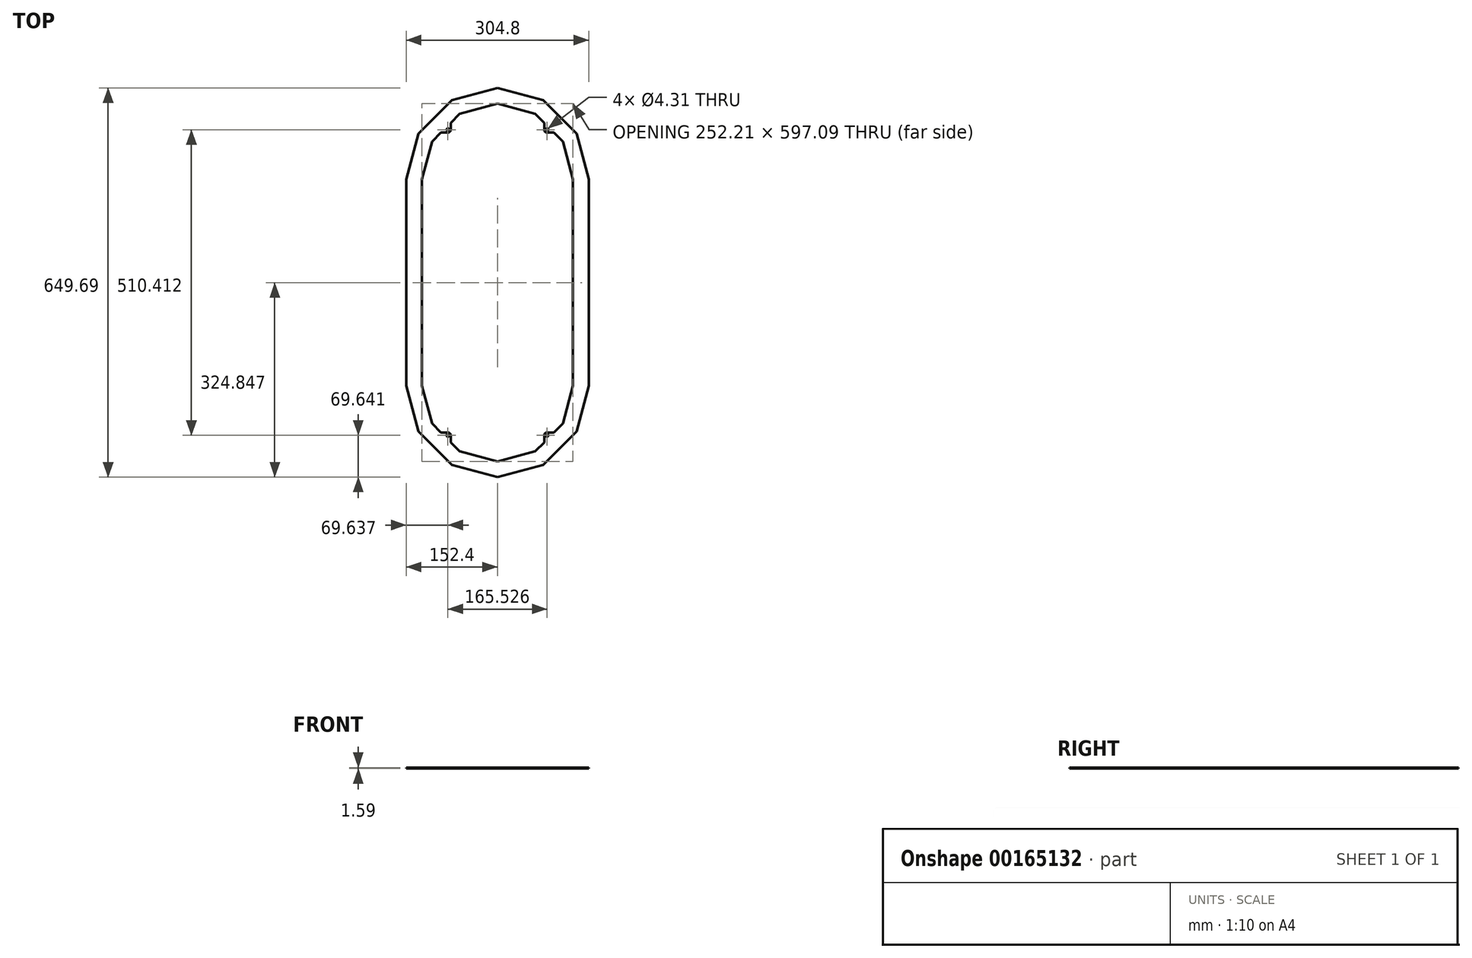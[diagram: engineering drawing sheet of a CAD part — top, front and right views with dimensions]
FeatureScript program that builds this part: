
annotation { "Feature Type Name" : "Feature", "Feature Type Description" : "" }
export const myFeature = defineFeature(function(context is Context, id is Id, definition is map)
    precondition{}
    {
        {
            var Q0;
            Q0=qCreatedBy(makeId("Top.planeOp"),FACE);
            var sketch = newSketch(context, id + "F0", { "sketchPlane" : qUnion([Q0])});
            skLineSegment(sketch, "E0", {"start": v(152.4, 0) * mm, "end": v(304.8, 0) * mm, "construction": true});
            skLineSegment(sketch, "E1", {"start": v(152.4, 0) * mm, "end": v(284.38, 76.2) * mm, "construction": true});
            skLineSegment(sketch, "E2", {"start": v(152.4, 0) * mm, "end": v(228.6, 131.98) * mm, "construction": true});
            skLineSegment(sketch, "E3", {"start": v(152.4, 0) * mm, "end": v(152.4, 152.4) * mm, "construction": true});
            skLineSegment(sketch, "E4", {"start": v(304.8, 0) * mm, "end": v(284.38, 76.2) * mm});
            skLineSegment(sketch, "E5", {"start": v(284.38, 76.2) * mm, "end": v(228.6, 131.98) * mm});
            skLineSegment(sketch, "E6", {"start": v(228.6, 131.98) * mm, "end": v(152.4, 152.4) * mm});
            skLineSegment(sketch, "E7", {"start": v(304.8, 0) * mm, "end": v(304.8, -344.89) * mm});
            skLineSegment(sketch, "E8", {"start": v(304.8, -344.89) * mm, "end": v(152.4, -344.89) * mm, "construction": true});
            skLineSegment(sketch, "E9", {"start": v(152.4, -344.89) * mm, "end": v(284.38, -421.09) * mm, "construction": true});
            skLineSegment(sketch, "E10", {"start": v(152.4, 0) * mm, "end": v(76.2, 131.98) * mm, "construction": true});
            skLineSegment(sketch, "E11", {"start": v(152.4, 0) * mm, "end": v(20.42, 76.2) * mm, "construction": true});
            skLineSegment(sketch, "E12", {"start": v(152.4, 0) * mm, "end": v(0, 0) * mm, "construction": true});
            skLineSegment(sketch, "E13", {"start": v(152.4, -344.89) * mm, "end": v(0, -344.89) * mm, "construction": true});
            skLineSegment(sketch, "E14", {"start": v(152.4, 152.4) * mm, "end": v(76.2, 131.98) * mm});
            skLineSegment(sketch, "E15", {"start": v(76.2, 131.98) * mm, "end": v(20.42, 76.2) * mm});
            skLineSegment(sketch, "E16", {"start": v(20.42, 76.2) * mm, "end": v(0, 0) * mm});
            skLineSegment(sketch, "E17", {"start": v(0, 0) * mm, "end": v(0, -344.89) * mm});
            skLineSegment(sketch, "E18", {"start": v(152.4, -344.89) * mm, "end": v(228.6, -476.87) * mm, "construction": true});
            skLineSegment(sketch, "E19", {"start": v(152.4, -344.89) * mm, "end": v(152.4, -497.29) * mm, "construction": true});
            skLineSegment(sketch, "E20", {"start": v(152.4, -344.89) * mm, "end": v(76.2, -476.87) * mm, "construction": true});
            skLineSegment(sketch, "E21", {"start": v(152.4, -344.89) * mm, "end": v(20.42, -421.09) * mm, "construction": true});
            skLineSegment(sketch, "E22", {"start": v(0, -344.89) * mm, "end": v(20.42, -421.09) * mm});
            skLineSegment(sketch, "E23", {"start": v(20.42, -421.09) * mm, "end": v(76.2, -476.87) * mm});
            skLineSegment(sketch, "E24", {"start": v(76.2, -476.87) * mm, "end": v(152.4, -497.29) * mm});
            skLineSegment(sketch, "E25", {"start": v(152.4, -497.29) * mm, "end": v(228.6, -476.87) * mm});
            skLineSegment(sketch, "E26", {"start": v(228.6, -476.87) * mm, "end": v(284.38, -421.09) * mm});
            skLineSegment(sketch, "E27", {"start": v(284.38, -421.09) * mm, "end": v(304.8, -344.89) * mm});
            skLineSegment(sketch, "E28", {"start": v(152.4, 0) * mm, "end": v(152.4, -172.44) * mm, "construction": true});
            skLineSegment(sketch, "E29", {"start": v(152.4, -172.44) * mm, "end": v(152.4, -344.89) * mm, "construction": true});
            skSolve(sketch);
        }
        {
            var Q0;
            Q0=qSketchRegion(id+"F0",true);
            extrude(context, id + "F1", {"entities" : qUnion([Q0]), "depth" : 1.59 * mm});
        }
        {
            var Q0;
            Q0=makeQuery(id+"F1.opExtrude","CAP_FACE",FACE,{"disambiguationData":[OSD([sQuery(id+"F0.wireOp",EDGE,"E4"),sQuery(id+"F0.wireOp",EDGE,"E5"),sQuery(id+"F0.wireOp",EDGE,"E6"),sQuery(id+"F0.wireOp",EDGE,"E7"),sQuery(id+"F0.wireOp",EDGE,"E14"),sQuery(id+"F0.wireOp",EDGE,"E15"),sQuery(id+"F0.wireOp",EDGE,"E16"),sQuery(id+"F0.wireOp",EDGE,"E17"),sQuery(id+"F0.wireOp",EDGE,"E22"),sQuery(id+"F0.wireOp",EDGE,"E23"),sQuery(id+"F0.wireOp",EDGE,"E24"),sQuery(id+"F0.wireOp",EDGE,"E25"),sQuery(id+"F0.wireOp",EDGE,"E26"),sQuery(id+"F0.wireOp",EDGE,"E27")])],"isStart":false});
            var sketch = newSketch(context, id + "F2", { "sketchPlane" : qUnion([Q0])});
            skLineSegment(sketch, "E30", {"start": v(152.4, 0) * mm, "end": v(278.5, 0) * mm, "construction": true});
            skLineSegment(sketch, "E31", {"start": v(152.4, 0) * mm, "end": v(261.6, 63.05) * mm, "construction": true});
            skLineSegment(sketch, "E32", {"start": v(152.4, 0) * mm, "end": v(215.45, 109.2) * mm, "construction": true});
            skLineSegment(sketch, "E33", {"start": v(152.4, 0) * mm, "end": v(152.4, 126.1) * mm, "construction": true});
            skLineSegment(sketch, "E34", {"start": v(278.5, 0) * mm, "end": v(261.6, 63.05) * mm});
            skLineSegment(sketch, "E35", {"start": v(261.6, 63.05) * mm, "end": v(215.45, 109.2) * mm});
            skLineSegment(sketch, "E36", {"start": v(215.45, 109.2) * mm, "end": v(152.4, 126.1) * mm});
            skLineSegment(sketch, "E37", {"start": v(278.5, 0) * mm, "end": v(278.5, -344.89) * mm});
            skLineSegment(sketch, "E38", {"start": v(278.5, -344.89) * mm, "end": v(152.4, -344.89) * mm, "construction": true});
            skLineSegment(sketch, "E39", {"start": v(152.4, -344.89) * mm, "end": v(261.6, -407.94) * mm, "construction": true});
            skLineSegment(sketch, "E40", {"start": v(152.4, 0) * mm, "end": v(89.35, 109.2) * mm, "construction": true});
            skLineSegment(sketch, "E41", {"start": v(152.4, 0) * mm, "end": v(43.2, 63.05) * mm, "construction": true});
            skLineSegment(sketch, "E42", {"start": v(152.4, 0) * mm, "end": v(26.3, 0) * mm, "construction": true});
            skLineSegment(sketch, "E43", {"start": v(152.4, -344.89) * mm, "end": v(26.3, -344.89) * mm, "construction": true});
            skLineSegment(sketch, "E44", {"start": v(152.4, 126.1) * mm, "end": v(89.35, 109.2) * mm});
            skLineSegment(sketch, "E45", {"start": v(89.35, 109.2) * mm, "end": v(43.2, 63.05) * mm});
            skLineSegment(sketch, "E46", {"start": v(43.2, 63.05) * mm, "end": v(26.3, 0) * mm});
            skLineSegment(sketch, "E47", {"start": v(26.3, 0) * mm, "end": v(26.3, -344.89) * mm});
            skLineSegment(sketch, "E48", {"start": v(152.4, -344.89) * mm, "end": v(215.45, -454.1) * mm, "construction": true});
            skLineSegment(sketch, "E49", {"start": v(152.4, -344.89) * mm, "end": v(152.4, -471) * mm, "construction": true});
            skLineSegment(sketch, "E50", {"start": v(152.4, -344.89) * mm, "end": v(89.35, -454.1) * mm, "construction": true});
            skLineSegment(sketch, "E51", {"start": v(152.4, -344.89) * mm, "end": v(43.2, -407.94) * mm, "construction": true});
            skLineSegment(sketch, "E52", {"start": v(26.3, -344.89) * mm, "end": v(43.2, -407.94) * mm});
            skLineSegment(sketch, "E53", {"start": v(43.2, -407.94) * mm, "end": v(89.35, -454.1) * mm});
            skLineSegment(sketch, "E54", {"start": v(89.35, -454.1) * mm, "end": v(152.4, -471) * mm});
            skLineSegment(sketch, "E55", {"start": v(152.4, -471) * mm, "end": v(215.45, -454.1) * mm});
            skLineSegment(sketch, "E56", {"start": v(215.45, -454.1) * mm, "end": v(261.6, -407.94) * mm});
            skLineSegment(sketch, "E57", {"start": v(261.6, -407.94) * mm, "end": v(278.5, -344.89) * mm});
            skLineSegment(sketch, "E58", {"start": v(152.4, 0) * mm, "end": v(152.4, -172.44) * mm, "construction": true});
            skLineSegment(sketch, "E59", {"start": v(152.4, -172.44) * mm, "end": v(152.4, -344.89) * mm, "construction": true});
            skLineSegment(sketch, "E60", {"start": v(270.06, -376.41) * mm, "end": v(294.6, -382.99) * mm, "construction": true});
            skLineSegment(sketch, "E61", {"start": v(34.74, -376.41) * mm, "end": v(10.2, -382.99) * mm, "construction": true});
            skLineSegment(sketch, "E62", {"start": v(34.74, 31.53) * mm, "end": v(10.2, 38.1) * mm, "construction": true});
            skLineSegment(sketch, "E63", {"start": v(270.06, 31.53) * mm, "end": v(294.6, 38.1) * mm, "construction": true});
            skSolve(sketch);
        }
        {
            var Q0;
            Q0=qSketchRegion(id+"F2",true);
            var Q1;
            Q1=makeQuery(id+"F1.opExtrude","CAP_FACE",FACE,{"disambiguationData":[OSD([sQuery(id+"F0.wireOp",EDGE,"E4"),sQuery(id+"F0.wireOp",EDGE,"E5"),sQuery(id+"F0.wireOp",EDGE,"E6"),sQuery(id+"F0.wireOp",EDGE,"E7"),sQuery(id+"F0.wireOp",EDGE,"E14"),sQuery(id+"F0.wireOp",EDGE,"E15"),sQuery(id+"F0.wireOp",EDGE,"E16"),sQuery(id+"F0.wireOp",EDGE,"E17"),sQuery(id+"F0.wireOp",EDGE,"E22"),sQuery(id+"F0.wireOp",EDGE,"E23"),sQuery(id+"F0.wireOp",EDGE,"E24"),sQuery(id+"F0.wireOp",EDGE,"E25"),sQuery(id+"F0.wireOp",EDGE,"E26"),sQuery(id+"F0.wireOp",EDGE,"E27")])],"isStart":true});
            extrude(context, id + "F3", {"entities" : qUnion([Q0]), "operationType" : NewBodyOperationType.REMOVE, "endBound" : BoundingType.UP_TO_SURFACE, "oppositeDirection" : true, "endBoundEntityFace" : qUnion([Q1]), "depth" : 25.4 * mm});
        }
        {
            var Q0;
            Q0=makeQuery(id+"F1.opExtrude","CAP_FACE",FACE,{"disambiguationData":[OSD([sQuery(id+"F0.wireOp",EDGE,"E4"),sQuery(id+"F0.wireOp",EDGE,"E5"),sQuery(id+"F0.wireOp",EDGE,"E6"),sQuery(id+"F0.wireOp",EDGE,"E7"),sQuery(id+"F0.wireOp",EDGE,"E14"),sQuery(id+"F0.wireOp",EDGE,"E15"),sQuery(id+"F0.wireOp",EDGE,"E16"),sQuery(id+"F0.wireOp",EDGE,"E17"),sQuery(id+"F0.wireOp",EDGE,"E22"),sQuery(id+"F0.wireOp",EDGE,"E23"),sQuery(id+"F0.wireOp",EDGE,"E24"),sQuery(id+"F0.wireOp",EDGE,"E25"),sQuery(id+"F0.wireOp",EDGE,"E26"),sQuery(id+"F0.wireOp",EDGE,"E27")])],"isStart":false});
            var sketch = newSketch(context, id + "F4", { "sketchPlane" : qUnion([Q0])});
            skLineSegment(sketch, "E64.bottom", {"start": v(235.16, 82.76) * mm, "end": v(69.64, 82.76) * mm, "construction": true});
            skLineSegment(sketch, "E64.top", {"start": v(235.16, -427.65) * mm, "end": v(69.64, -427.65) * mm, "construction": true});
            skLineSegment(sketch, "E64.left", {"start": v(235.16, 82.76) * mm, "end": v(235.16, -427.65) * mm, "construction": true});
            skLineSegment(sketch, "E64.right", {"start": v(69.64, 82.76) * mm, "end": v(69.64, -427.65) * mm, "construction": true});
            skPoint(sketch, "E64.middle", {"position": v(152.4, -172.44) * mm});
            skLineSegment(sketch, "E65", {"start": v(152.4, 126.1) * mm, "end": v(152.4, -471) * mm, "construction": true});
            skLineSegment(sketch, "E66.bottom", {"start": v(230.4, 94.26) * mm, "end": v(230.4, 82.76) * mm});
            skLineSegment(sketch, "E66.top", {"start": v(246.66, 78) * mm, "end": v(235.16, 78) * mm});
            skLineSegment(sketch, "E66.left", {"start": v(230.4, 94.26) * mm, "end": v(246.66, 78) * mm});
            skLineSegment(sketch, "E67.bottom", {"start": v(74.4, 82.76) * mm, "end": v(74.4, 94.26) * mm});
            skLineSegment(sketch, "E67.top", {"start": v(69.64, 78) * mm, "end": v(58.14, 78) * mm});
            skLineSegment(sketch, "E67.right", {"start": v(74.4, 94.26) * mm, "end": v(58.14, 78) * mm});
            skArc(sketch, "E68", {"start": v(69.64, 78) * mm, "mid": v(73, 79.4) * mm, "end": v(74.4, 82.76) * mm});
            skArc(sketch, "E69", {"start": v(230.4, 82.76) * mm, "mid": v(231.8, 79.4) * mm, "end": v(235.16, 78) * mm});
            skLineSegment(sketch, "E70.bottom", {"start": v(58.14, -422.89) * mm, "end": v(74.4, -439.15) * mm});
            skLineSegment(sketch, "E70.left", {"start": v(74.4, -439.15) * mm, "end": v(74.4, -427.65) * mm});
            skLineSegment(sketch, "E70.right", {"start": v(58.14, -422.89) * mm, "end": v(69.64, -422.89) * mm});
            skLineSegment(sketch, "E71.bottom", {"start": v(246.66, -422.89) * mm, "end": v(230.4, -439.15) * mm});
            skLineSegment(sketch, "E71.left", {"start": v(246.66, -422.89) * mm, "end": v(235.16, -422.89) * mm});
            skLineSegment(sketch, "E71.right", {"start": v(230.4, -439.15) * mm, "end": v(230.4, -427.65) * mm});
            skArc(sketch, "E72", {"start": v(74.4, -427.65) * mm, "mid": v(73, -424.28) * mm, "end": v(69.64, -422.89) * mm});
            skArc(sketch, "E73", {"start": v(235.16, -422.89) * mm, "mid": v(231.8, -424.28) * mm, "end": v(230.4, -427.65) * mm});
            skCircle(sketch, "E74", {"center": v(235.16, -427.65) * mm, "radius": 2.15 * mm});
            skCircle(sketch, "E75", {"center": v(69.64, -427.65) * mm, "radius": 2.15 * mm});
            skCircle(sketch, "E76", {"center": v(235.16, 82.76) * mm, "radius": 2.15 * mm});
            skCircle(sketch, "E77", {"center": v(69.64, 82.76) * mm, "radius": 2.15 * mm});
            skArc(sketch, "E78", {"start": v(69.64, -422.89) * mm, "mid": v(66.27, -431.02) * mm, "end": v(74.4, -427.65) * mm, "construction": true});
            skPoint(sketch, "E79", {"position": v(66.27, -431.02) * mm});
            skPoint(sketch, "E80", {"position": v(238.53, -431.02) * mm});
            skPoint(sketch, "E81", {"position": v(238.53, 86.13) * mm});
            skPoint(sketch, "E82", {"position": v(66.27, 86.13) * mm});
            skSolve(sketch);
        }
        {
            var Q0;
            Q0=qSketchRegion(id+"F4",true);
            var Q1;
            Q1=makeQuery(id+"F1.opExtrude","CAP_FACE",FACE,{"disambiguationData":[OSD([sQuery(id+"F0.wireOp",EDGE,"E4"),sQuery(id+"F0.wireOp",EDGE,"E5"),sQuery(id+"F0.wireOp",EDGE,"E6"),sQuery(id+"F0.wireOp",EDGE,"E7"),sQuery(id+"F0.wireOp",EDGE,"E14"),sQuery(id+"F0.wireOp",EDGE,"E15"),sQuery(id+"F0.wireOp",EDGE,"E16"),sQuery(id+"F0.wireOp",EDGE,"E17"),sQuery(id+"F0.wireOp",EDGE,"E22"),sQuery(id+"F0.wireOp",EDGE,"E23"),sQuery(id+"F0.wireOp",EDGE,"E24"),sQuery(id+"F0.wireOp",EDGE,"E25"),sQuery(id+"F0.wireOp",EDGE,"E26"),sQuery(id+"F0.wireOp",EDGE,"E27")])],"isStart":true});
            extrude(context, id + "F5", {"entities" : qUnion([Q0]), "operationType" : NewBodyOperationType.ADD, "endBound" : BoundingType.UP_TO_SURFACE, "oppositeDirection" : true, "endBoundEntityFace" : qUnion([Q1]), "depth" : 25.4 * mm});
        }
    });
